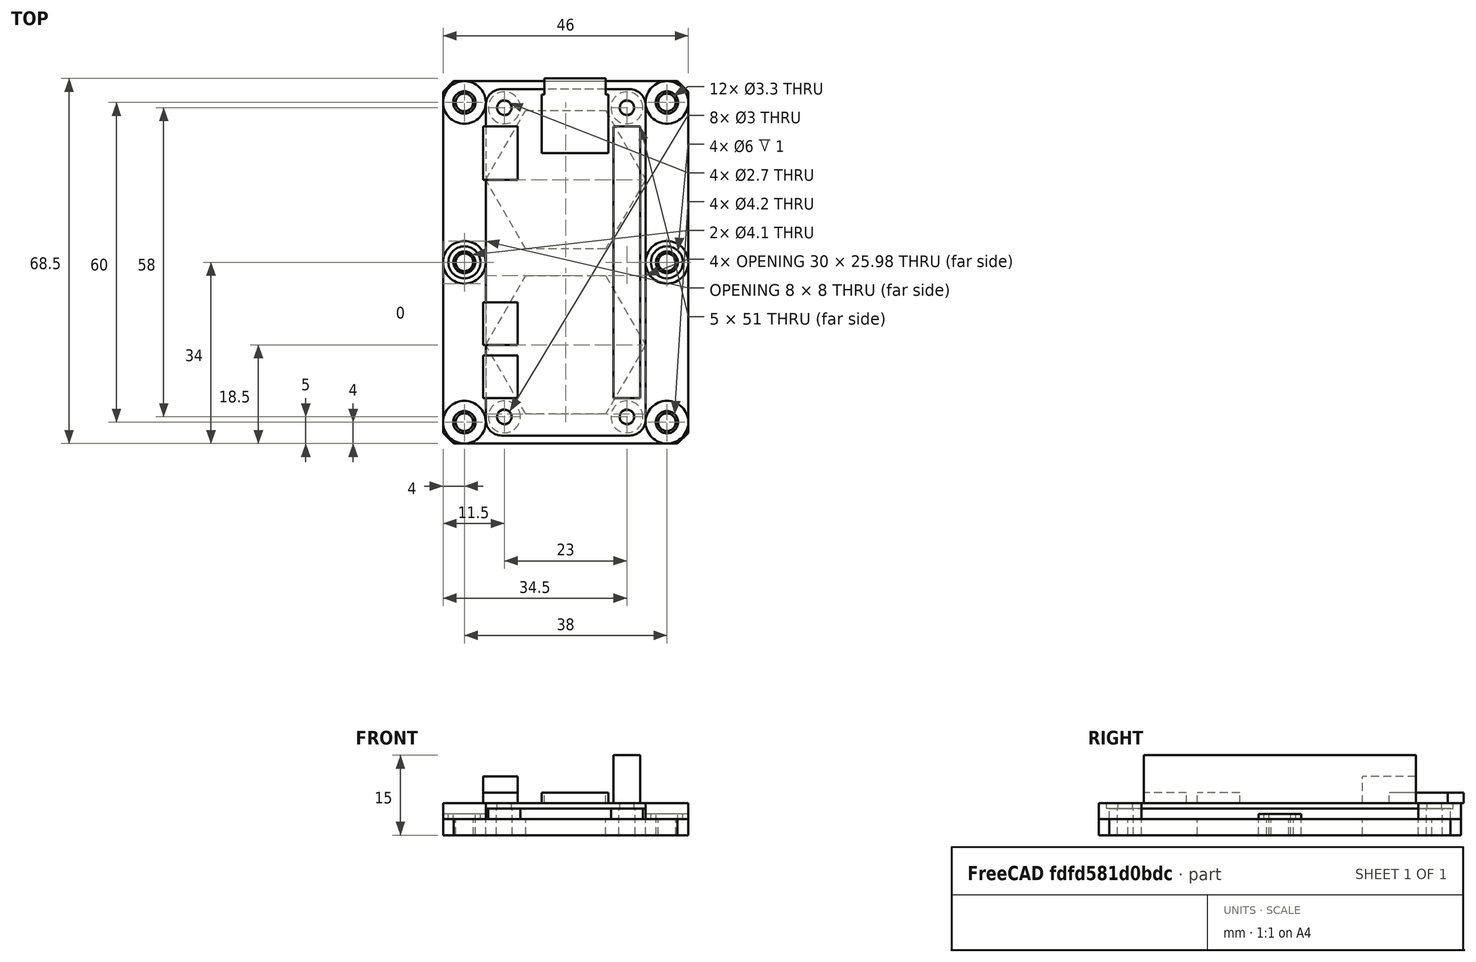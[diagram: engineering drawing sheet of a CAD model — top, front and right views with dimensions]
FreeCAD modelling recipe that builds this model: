
FCSTD DOCUMENT  (FreeCAD 0.18R16146 (Git))
Label: rpi-adapter
License: All rights reserved
LicenseURL: http://en.wikipedia.org/wiki/All_rights_reserved
objects: Part::Cylinder×30, Part::MultiFuse×16, Part::Box×8, Part::Cut×8, Part::Feature×6, Part::Fillet×1, Part::Chamfer×1
note: 70 computed .brp shape members not serialized (recipe doc carries the construction recipe); baked Part::Feature solids carry a one-line shape summary decoded from their .brp

FEATURE [Part::Box] Box  label="Cube"
  AttacherType = Attacher::AttachEngine3D
  Height = 1
  Length = 30
  Width = 65
FEATURE [Part::Fillet] Fillet
  Base = -> Box
  Edges = 4 edges r=3: [Edge1,Edge3,Edge5,Edge7]
FEATURE [Part::Cylinder] Cylinder
  Angle = 360
  AttacherType = Attacher::AttachEngine3D
  Height = 10
  Placement = pos=(3.5,3.5,0) rot=(0,0,1;0rad)
  Radius = 1.35
FEATURE [Part::Cylinder] Cylinder001
  Angle = 360
  AttacherType = Attacher::AttachEngine3D
  Height = 10
  Placement = pos=(3.5,61.5,0) rot=(0,0,1;0rad)
  Radius = 1.35
FEATURE [Part::Cylinder] Cylinder002
  Angle = 360
  AttacherType = Attacher::AttachEngine3D
  Height = 10
  Placement = pos=(26.5,61.5,0) rot=(0,0,1;0rad)
  Radius = 1.35
FEATURE [Part::Cylinder] Cylinder003
  Angle = 360
  AttacherType = Attacher::AttachEngine3D
  Height = 10
  Placement = pos=(26.5,3.5,0) rot=(0,0,1;0rad)
  Radius = 1.35
FEATURE [Part::Box] Box001  label="Cube001"
  AttacherType = Attacher::AttachEngine3D
  Height = 10
  Length = 5
  Placement = pos=(1,7,0) rot=(0,0,1;0rad)
  Width = 51
FEATURE [Part::Box] Box002  label="Cube002"
  AttacherType = Attacher::AttachEngine3D
  Height = 5
  Length = 6.5
  Placement = pos=(24,7,1) rot=(0,0,1;0rad)
  Width = 10
FEATURE [Part::Box] Box003  label="Cube003"
  AttacherType = Attacher::AttachEngine3D
  Height = 2
  Length = 6.5
  Placement = pos=(24,50,1) rot=(0,0,1;0rad)
  Width = 8
FEATURE [Part::Box] Box004  label="Cube004"
  AttacherType = Attacher::AttachEngine3D
  Height = 2
  Length = 6.5
  Placement = pos=(24,40,1) rot=(0,0,1;0rad)
  Width = 8
FEATURE [Part::Box] Box005  label="Cube005"
  AttacherType = Attacher::AttachEngine3D
  Height = 2
  Length = 12.5
  Placement = pos=(7,1,1) rot=(0,0,1;0rad)
  Width = 11
FEATURE [Part::Cylinder] Cylinder004
  Angle = 360
  AttacherType = Attacher::AttachEngine3D
  Height = 5
  Placement = pos=(26.5,3.5,0) rot=(0,0,1;0rad)
  Radius = 1.5
FEATURE [Part::Cylinder] Cylinder005
  Angle = 360
  AttacherType = Attacher::AttachEngine3D
  Height = 5
  Placement = pos=(26.5,61.5,0) rot=(0,0,1;0rad)
  Radius = 1.5
FEATURE [Part::Cylinder] Cylinder006
  Angle = 360
  AttacherType = Attacher::AttachEngine3D
  Height = 5
  Placement = pos=(3.5,61.5,0) rot=(0,0,1;0rad)
  Radius = 1.5
FEATURE [Part::Cylinder] Cylinder007
  Angle = 360
  AttacherType = Attacher::AttachEngine3D
  Height = 5
  Placement = pos=(3.5,3.5,0) rot=(0,0,1;0rad)
  Radius = 1.5
FEATURE [Part::MultiFuse] Fusion
  Shapes = -> [Cylinder003,Cylinder002,Cylinder001,Cylinder]
FEATURE [Part::Cut] Cut
  Base = -> Fillet
  Tool = -> Fusion
FEATURE [Part::Box] Box006  label="Cube006"
  AttacherType = Attacher::AttachEngine3D
  Height = 2
  Length = 11.5
  Placement = pos=(7.5,-2,1) rot=(0,0,1;0rad)
  Width = 11
FEATURE [Part::MultiFuse] Fusion002  label="Rpi-pref"
  Placement = pos=(3.6e-15,29,5) rot=(0,0,1;3.14159rad)
  Shapes = -> [Box006,Cut,Box005,Box001,Box002,Box003,Box004]
FEATURE [Part::Cylinder] Cylinder008
  Angle = 360
  AttacherType = Attacher::AttachEngine3D
  Height = 6
  Placement = pos=(4,26.5,0) rot=(0,0,1;0rad)
  Radius = 4
FEATURE [Part::Cylinder] Cylinder009
  Angle = 360
  AttacherType = Attacher::AttachEngine3D
  Height = 6
  Placement = pos=(-34,26.5,0) rot=(0,0,1;0rad)
  Radius = 4
FEATURE [Part::Cylinder] Cylinder010
  Angle = 360
  AttacherType = Attacher::AttachEngine3D
  Height = 6
  Placement = pos=(-34,-33.5,0) rot=(0,0,1;0rad)
  Radius = 4
FEATURE [Part::Cylinder] Cylinder011
  Angle = 360
  AttacherType = Attacher::AttachEngine3D
  Height = 6
  Placement = pos=(4,-33.5,0) rot=(0,0,1;0rad)
  Radius = 4
FEATURE [Part::Box] Box007  label="Cube007"
  AttacherType = Attacher::AttachEngine3D
  Height = 3
  Length = 46
  Placement = pos=(-38,-37.5,0) rot=(0,0,1;0rad)
  Width = 68
FEATURE [Part::Cylinder] Cylinder013
  Angle = 360
  AttacherType = Attacher::AttachEngine3D
  Height = 10
  Placement = pos=(4,-3.5,0) rot=(0,0,1;0rad)
  Radius = 1.65
FEATURE [Part::Cylinder] Cylinder014
  Angle = 360
  AttacherType = Attacher::AttachEngine3D
  Height = 10
  Placement = pos=(-34,-3.5,0) rot=(0,0,1;0rad)
  Radius = 1.65
FEATURE [Part::Cylinder] Cylinder015
  Angle = 360
  AttacherType = Attacher::AttachEngine3D
  Height = 4
  Placement = pos=(-34,-3.5,0) rot=(0,0,1;0rad)
  Radius = 2.05
FEATURE [Part::Cylinder] Cylinder016
  Angle = 360
  AttacherType = Attacher::AttachEngine3D
  Height = 4
  Placement = pos=(4,-3.5,0) rot=(0,0,1;0rad)
  Radius = 2.05
FEATURE [Part::Cylinder] Cylinder019
  Angle = 360
  AttacherType = Attacher::AttachEngine3D
  Height = 4
  Placement = pos=(4,-3.5,0) rot=(0,0,1;0rad)
  Radius = 4
FEATURE [Part::Cylinder] Cylinder020
  Angle = 360
  AttacherType = Attacher::AttachEngine3D
  Height = 4
  Placement = pos=(-34,-3.5,0) rot=(0,0,1;0rad)
  Radius = 4
FEATURE [Part::Cylinder] Cylinder021
  Angle = 360
  AttacherType = Attacher::AttachEngine3D
  Height = 4
  Placement = pos=(4,-3.5,0) rot=(0,0,1;0rad)
  Radius = 4
FEATURE [Part::Cylinder] Cylinder023
  Angle = 360
  AttacherType = Attacher::AttachEngine3D
  Height = 4
  Placement = pos=(-34,-3.5,0) rot=(0,0,1;0rad)
  Radius = 4
FEATURE [Part::Cylinder] Cylinder024
  Angle = 360
  AttacherType = Attacher::AttachEngine3D
  Height = 1
  Placement = pos=(-34,-3.5,3) rot=(0,0,1;0rad)
  Radius = 3
FEATURE [Part::Cylinder] Cylinder025
  Angle = 360
  AttacherType = Attacher::AttachEngine3D
  Height = 1
  Placement = pos=(4,-3.5,3) rot=(0,0,1;0rad)
  Radius = 3
FEATURE [Part::Cylinder] Cylinder027
  Angle = 360
  AttacherType = Attacher::AttachEngine3D
  Height = 6
  Placement = pos=(4,-33.5,0) rot=(0,0,1;0rad)
  Radius = 1.65
FEATURE [Part::Cylinder] Cylinder028
  Angle = 360
  AttacherType = Attacher::AttachEngine3D
  Height = 6
  Placement = pos=(4,26.5,0) rot=(0,0,1;0rad)
  Radius = 1.65
FEATURE [Part::Cylinder] Cylinder029
  Angle = 360
  AttacherType = Attacher::AttachEngine3D
  Height = 6
  Placement = pos=(-34,26.5,0) rot=(0,0,1;0rad)
  Radius = 1.65
FEATURE [Part::Cylinder] Cylinder030
  Angle = 360
  AttacherType = Attacher::AttachEngine3D
  Height = 6
  Placement = pos=(-34,-33.5,0) rot=(0,0,1;0rad)
  Radius = 1.65
FEATURE [Part::MultiFuse] Fusion010
  Shapes = -> [Cylinder011,Cylinder008,Cylinder009,Cylinder010]
FEATURE [Part::Cylinder] Cylinder031
  Angle = 360
  AttacherType = Attacher::AttachEngine3D
  Height = 5
  Placement = pos=(26.5,3.5,0) rot=(0,0,1;0rad)
  Radius = 3
FEATURE [Part::Cylinder] Cylinder032
  Angle = 360
  AttacherType = Attacher::AttachEngine3D
  Height = 5
  Placement = pos=(26.5,61.5,0) rot=(0,0,1;0rad)
  Radius = 3
FEATURE [Part::Cylinder] Cylinder033
  Angle = 360
  AttacherType = Attacher::AttachEngine3D
  Height = 5
  Placement = pos=(3.5,61.5,0) rot=(0,0,1;0rad)
  Radius = 3
FEATURE [Part::Cylinder] Cylinder034
  Angle = 360
  AttacherType = Attacher::AttachEngine3D
  Height = 5
  Placement = pos=(3.5,3.5,0) rot=(0,0,1;0rad)
  Radius = 3
FEATURE [Part::MultiFuse] Fusion012
  Placement = pos=(-30,-36,0) rot=(0,0,1;0rad)
  Shapes = -> [Cylinder034,Cylinder033,Cylinder032,Cylinder031]
FEATURE [Part::MultiFuse] Fusion013
  Placement = pos=(-30,-36,0) rot=(0,0,1;0rad)
  Shapes = -> [Cylinder004,Cylinder007,Cylinder006,Cylinder005]
FEATURE [Part::MultiFuse] Fusion014
  Shapes = -> [Cylinder021,Cylinder023]
FEATURE [Part::MultiFuse] Fusion015
  Shapes = -> [Cylinder013,Cylinder014]
FEATURE [Part::MultiFuse] Fusion016
  Shapes = -> [Cylinder024,Cylinder025]
FEATURE [Part::Cut] Cut002
  Base = -> Fusion014
  Tool = -> Fusion016
FEATURE [Part::MultiFuse] Fusion017
  Shapes = -> [Box007,Cut002]
FEATURE [Part::Cut] Cut003
  Base = -> Fusion017
  Tool = -> Fusion015
FEATURE [Part::MultiFuse] Fusion018
  Shapes = -> [Cylinder019,Cylinder020]
FEATURE [Part::MultiFuse] Fusion019
  Shapes = -> [Cylinder016,Cylinder015]
FEATURE [Part::Cut] Cut004
  Base = -> Fusion018
  Tool = -> Fusion019
FEATURE [Part::Feature] Fusion010001  label="Fusion020"
  shape: bbox 46 x 68 x 6 mm, 12 faces, 4 solids (baked)
FEATURE [Part::Feature] Fusion009001  label="Fusion021"
  shape: bbox 42.2 x 64.2 x 6 mm, 12 faces, 4 solids (baked)
FEATURE [Part::Cut] Cut005
  Base = -> Fusion010001
  Tool = -> Fusion009001
FEATURE [Part::MultiFuse] Fusion010002  label="board-mounter-slot"
  Shapes = -> [Cut005,Cut004]
FEATURE [Part::MultiFuse] Fusion010003
  Shapes = -> [Cylinder027,Cylinder028,Cylinder029,Cylinder030]
FEATURE [Part::MultiFuse] Fusion010004
  Shapes = -> [Cut003,Fusion010]
FEATURE [Part::Cut] Cut006
  Base = -> Fusion010004
  Tool = -> Fusion010003
FEATURE [Part::Chamfer] Chamfer
  Base = -> Cut006
  Edges = 4 edges r=2: [Edge4,Edge66,Edge78,Edge83]
FEATURE [Part::MultiFuse] Fusion010005
  Shapes = -> [Chamfer,Fusion012]
FEATURE [Part::Cut] Cut007
  Base = -> Fusion010005
  Tool = -> Fusion013
FEATURE [Part::Feature] Body001
  Placement = pos=(-15,-4,0) rot=(0,0,1;4.71239rad)
  shape: bbox 30 x 25.98 x 10 mm, 8 faces (baked)
FEATURE [Part::Feature] Body002
  Placement = pos=(-15,-35,0) rot=(0,0,-1;1.5708rad)
  shape: bbox 30 x 25.98 x 10 mm, 8 faces (baked)
FEATURE [Part::MultiFuse] Fusion010006
  Shapes = -> [Body002,Body001]
FEATURE [Part::Cut] Cut008
  Base = -> Cut007
  Tool = -> Fusion010006
FEATURE [Part::Feature] Fusion010002001  label="board-mounter-slot001"
  shape: bbox 46 x 68 x 6 mm, 24 faces, 6 solids (baked)
FEATURE [Part::Feature] Cut008001  label="pi-mounter-pred"
  shape: bbox 46 x 68 x 6 mm, 60 faces (baked)
